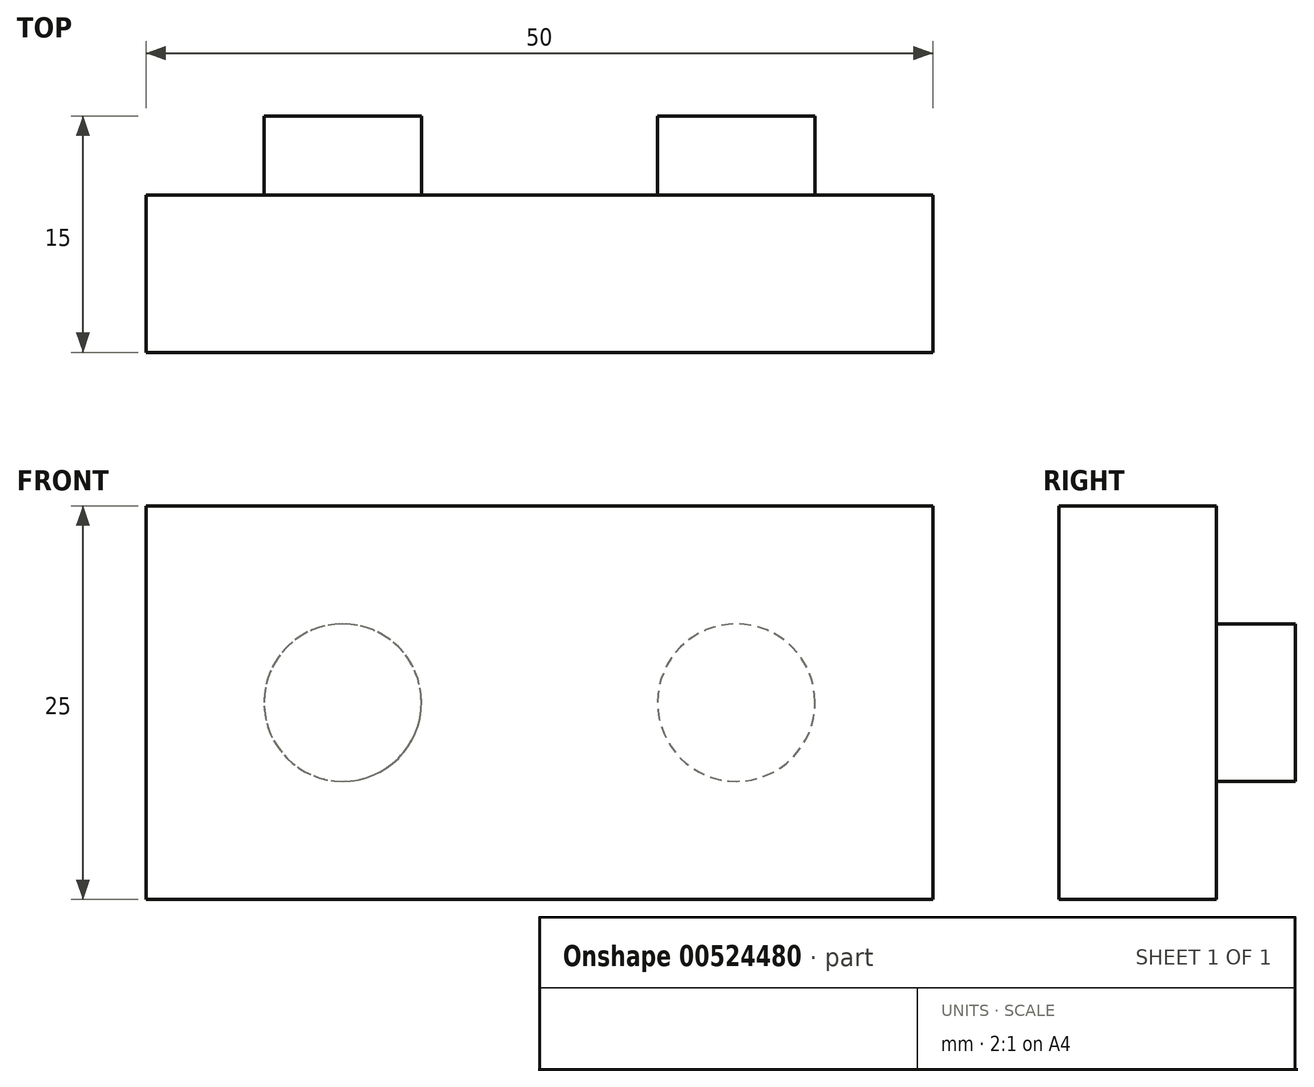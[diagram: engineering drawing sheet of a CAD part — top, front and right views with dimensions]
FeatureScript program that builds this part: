
annotation { "Feature Type Name" : "Feature", "Feature Type Description" : "" }
export const myFeature = defineFeature(function(context is Context, id is Id, definition is map)
    precondition{}
    {
        {
            var Q0;
            Q0=qCreatedBy(makeId("Front.planeOp"),FACE);
            var sketch = newSketch(context, id + "F0", { "sketchPlane" : qUnion([Q0])});
            skLineSegment(sketch, "E0.bottom", {"start": v(25, 12.5) * mm, "end": v(-25, 12.5) * mm});
            skLineSegment(sketch, "E0.top", {"start": v(25, -12.5) * mm, "end": v(-25, -12.5) * mm});
            skLineSegment(sketch, "E0.left", {"start": v(25, 12.5) * mm, "end": v(25, -12.5) * mm});
            skLineSegment(sketch, "E0.right", {"start": v(-25, 12.5) * mm, "end": v(-25, -12.5) * mm});
            skPoint(sketch, "E0.middle", {"position": v(0, 0) * mm});
            skSolve(sketch);
        }
        {
            var Q0;
            Q0 = qSketchRegion(id + "F0", true);
            extrude(context, id + "F1", {"entities" : qUnion([Q0]), "depth" : 10 * mm, "offsetDistance" : 25 * mm});
        }
        {
            var Q0;
            Q0=makeQuery(id+"F1.opExtrude","CAP_FACE",FACE,{"disambiguationData":[OSD([sQuery(id+"F0.wireOp",EDGE,"E0.bottom"),sQuery(id+"F0.wireOp",EDGE,"E0.top"),sQuery(id+"F0.wireOp",EDGE,"E0.left"),sQuery(id+"F0.wireOp",EDGE,"E0.right")])],"isStart":true});
            var sketch = newSketch(context, id + "F2", { "sketchPlane" : qUnion([Q0])});
            skLineSegment(sketch, "E1", {"start": v(0, 0) * mm, "end": v(25, 0) * mm, "construction": true});
            skLineSegment(sketch, "E2", {"start": v(0, 0) * mm, "end": v(-25, 0) * mm, "construction": true});
            skLineSegment(sketch, "E3", {"start": v(12.5, 0) * mm, "end": v(12.5, 12.5) * mm, "construction": true});
            skLineSegment(sketch, "E4", {"start": v(-12.5, 0) * mm, "end": v(-12.5, 12.5) * mm, "construction": true});
            skCircle(sketch, "E5", {"center": v(-12.5, 0) * mm, "radius": 5 * mm});
            skCircle(sketch, "E6", {"center": v(12.5, 0) * mm, "radius": 5 * mm});
            skSolve(sketch);
        }
        {
            var Q0;
            Q0 = qSketchRegion(id + "F2", true);
            extrude(context, id + "F3", {"entities" : qUnion([Q0]), "operationType" : NewBodyOperationType.ADD, "depth" : 5 * mm, "offsetDistance" : 25 * mm});
        }
    });
